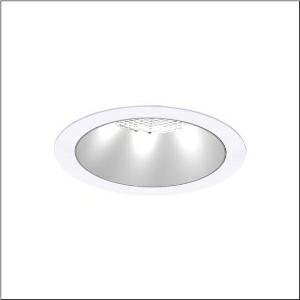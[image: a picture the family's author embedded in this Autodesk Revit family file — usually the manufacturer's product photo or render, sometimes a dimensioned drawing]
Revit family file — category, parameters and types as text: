
# Revit family: lunis_21_xl_51db19mf91c
name_source: partatom
category: Lighting Fixtures
units: mm (PartAtom-declared; Revit-internal decimal feet)

## family parameters
Cut with Voids When Loaded = No
Host = Face
Light Source = No
Part Type = Normal
Room Calculation Point = No
Round Connector Dimension = Use Diameter
Shared = No

## types (1)
- --- (1 x LED, 3560 lm, 21.7 W, 6500K)
    Apparent Load = 22 VA
    CIE Flux Codes = 91 99 100 100 100
    Color Rendering = 80
    Color Temperature = 6500K
    Default Elevation = 1800 mm
    Description = Lunis 21 XL, downlight, light control with lens, of PMMA, anti glare with reflector, of PC, matt, light emission: direct distribution, LED rated luminous flux: 2.390lm, light colour: 830/840/865, with terminal, 3-pole, mains connection: 220..240V, AC/DC, 0/50..60Hz, housing, round, of diecast aluminium, traffic white (RAL 9016), diameter: 230mm, clamping range: 1..40mm, protection rating (complete): IP20, protection rating (on room side): IP54, insulation class (complete): insulation class II (safety insulation), certification: CE, impact resistance: IK03, packaging unit: 1 piece
    Height = 0 mm  [stored 0 ft]
    Lamp = 1 x LED
    Lamp Light Flux = 3560 lm
    Lamp Power = 21.7 W
    Lamp count = 1
    Length = 230 mm
    Luminous efficacy = 164 lm/W
    Manufacturer = Siteco
    ModVariant = No
    Model = 51DB19MF91C
    Mounting Place = Ceiling
    Mounting Type = Recessed
    Number of Poles = 1
    OnlyDefault = Yes
    Power Factor = 1
    Product Name = Lunis 21 XL
    Product group = downlight
    ProductGroupID = 401
    Protection Class = Protection class II
    Protection Degree = IP 20
    RLX_Detail_Level = 1
    RLX_Emergency_Light_Flux = 0 lm
    RLX_Emergency_Type = 0
    RLX_Emergency_Type_DB = No
    RlxData = <blob elided: 20921 chars, md5=0b5d2182>
    Socket = socket
    Standby Power = 0 W
    System Light Flux = 3560 lm
    System Power = 22 W
    Type Comments = individual setting: colour temperature 6500K, luminous flux: 100 % | (OFF | ON | ON | ON) | 650 mA
    Type Image = l_1291163.jpg
    URL = http://relux.com
    VarID = @adj_034651
    Voltage = 0 V
    Weight = 0.00 kg
    Width = 0 mm  [stored 0 ft]

note: [stored X ft] marks values corroborated as IEEE doubles in the binary element streams (Revit-internal decimal feet)

## geometry (parser evidence)
native form markers: Blend x4, Sweep x11
no freeform markers — native parametric forms only
